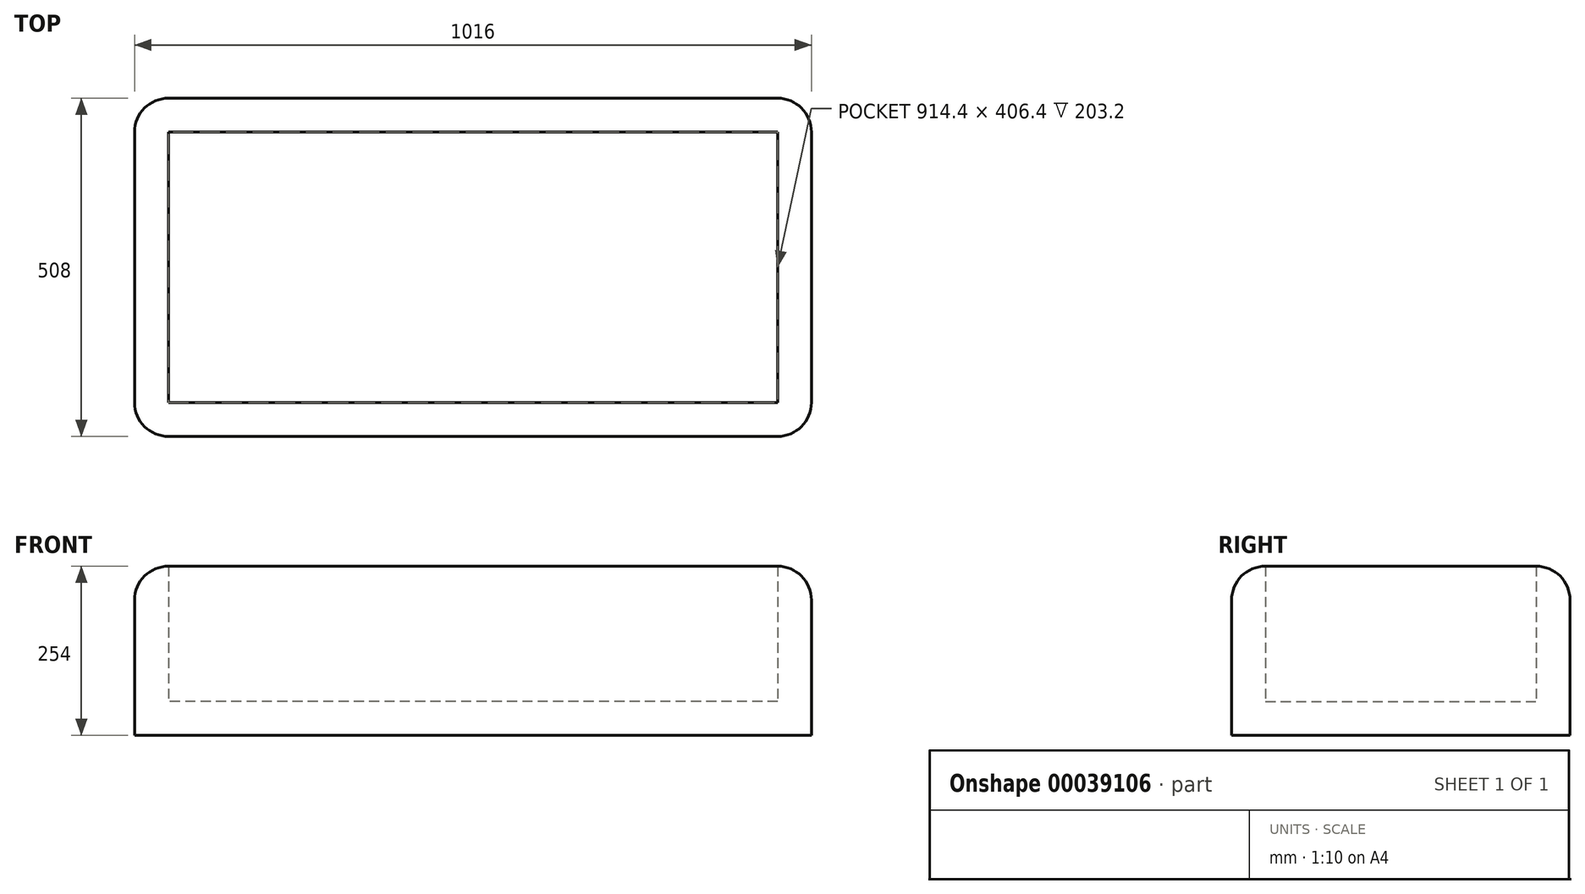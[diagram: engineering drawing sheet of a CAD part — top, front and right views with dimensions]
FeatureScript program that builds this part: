
annotation { "Feature Type Name" : "Feature", "Feature Type Description" : "" }
export const myFeature = defineFeature(function(context is Context, id is Id, definition is map)
    precondition{}
    {
        {
            var Q0;
            Q0=qCreatedBy(makeId("Top.planeOp"),FACE);
            var sketch = newSketch(context, id + "F0", { "sketchPlane" : qUnion([Q0])});
            skLineSegment(sketch, "E0.bottom", {"start": v(966.31, 0) * mm, "end": v(-49.69, 0) * mm});
            skLineSegment(sketch, "E0.top", {"start": v(966.31, 508) * mm, "end": v(-49.69, 508) * mm});
            skLineSegment(sketch, "E0.left", {"start": v(966.31, 0) * mm, "end": v(966.31, 508) * mm});
            skLineSegment(sketch, "E0.right", {"start": v(-49.69, 0) * mm, "end": v(-49.69, 508) * mm});
            skLineSegment(sketch, "E1.bottom", {"start": v(0, 0) * mm, "end": v(0, 0) * mm});
            skSolve(sketch);
        }
        {
            var Q0;
            Q0=makeQuery(id+"F0.imprint","IMPRINT",FACE,{"disambiguationData":[TD([[makeQuery(id+"F0.imprint","IMPRINT",EDGE,{"derivedFrom":sQuery(id+"F0.wireOp",EDGE,"E0.bottom")}),-1.0]])]});
            extrude(context, id + "F1", {"entities" : qUnion([Q0]), "depth" : 254 * mm});
        }
        {
            var Q0;
            Q0=makeQuery(id+"F1.opExtrude","CAP_FACE",FACE,{"disambiguationData":[OSD([sQuery(id+"F0.wireOp",EDGE,"E0.bottom"),sQuery(id+"F0.wireOp",EDGE,"E0.top"),sQuery(id+"F0.wireOp",EDGE,"E0.left"),sQuery(id+"F0.wireOp",EDGE,"E0.right")])],"isStart":false});
            shell(context, id + "F2", {"entities" : qUnion([Q0]), "thickness" : 50.8 * mm});
        }
        {
            var Q0;
            Q0=makeQuery(id+"F1.opExtrude","SWEPT_EDGE",EDGE,{"disambiguationData":[OSD([sQuery(id+"F0.wireOp",EDGE,"E0.bottom"),sQuery(id+"F0.wireOp",EDGE,"E0.right")])]});
            var Q1;
            Q1=makeQuery(id+"F1.opExtrude","SWEPT_EDGE",EDGE,{"disambiguationData":[OSD([sQuery(id+"F0.wireOp",EDGE,"E0.bottom"),sQuery(id+"F0.wireOp",EDGE,"E0.left")])]});
            var Q2;
            Q2=makeQuery(id+"F1.opExtrude","SWEPT_EDGE",EDGE,{"disambiguationData":[OSD([sQuery(id+"F0.wireOp",EDGE,"E0.top"),sQuery(id+"F0.wireOp",EDGE,"E0.left")])]});
            var Q3;
            Q3=makeQuery(id+"F1.opExtrude","CAP_EDGE",EDGE,{"disambiguationData":[OSD([sQuery(id+"F0.wireOp",EDGE,"E0.top")])],"isStart":false});
            var Q4;
            Q4=makeQuery(id+"F1.opExtrude","CAP_EDGE",EDGE,{"disambiguationData":[OSD([sQuery(id+"F0.wireOp",EDGE,"E0.bottom")])],"isStart":false});
            var Q5;
            Q5=makeQuery(id+"F1.opExtrude","CAP_EDGE",EDGE,{"disambiguationData":[OSD([sQuery(id+"F0.wireOp",EDGE,"E0.left")])],"isStart":false});
            var Q6;
            Q6=makeQuery(id+"F1.opExtrude","CAP_EDGE",EDGE,{"disambiguationData":[OSD([sQuery(id+"F0.wireOp",EDGE,"E0.right")])],"isStart":false});
            var Q7;
            Q7=makeQuery(id+"F1.opExtrude","SWEPT_EDGE",EDGE,{"disambiguationData":[OSD([sQuery(id+"F0.wireOp",EDGE,"E0.top"),sQuery(id+"F0.wireOp",EDGE,"E0.right")])]});
            fillet(context, id + "F3", {"entities" : qUnion([Q0, Q1, Q2, Q3, Q4, Q5, Q6, Q7]), "radius" : 50.8 * mm, "tangentPropagation" : true, "allowEdgeOverflow" : false});
        }
    });
